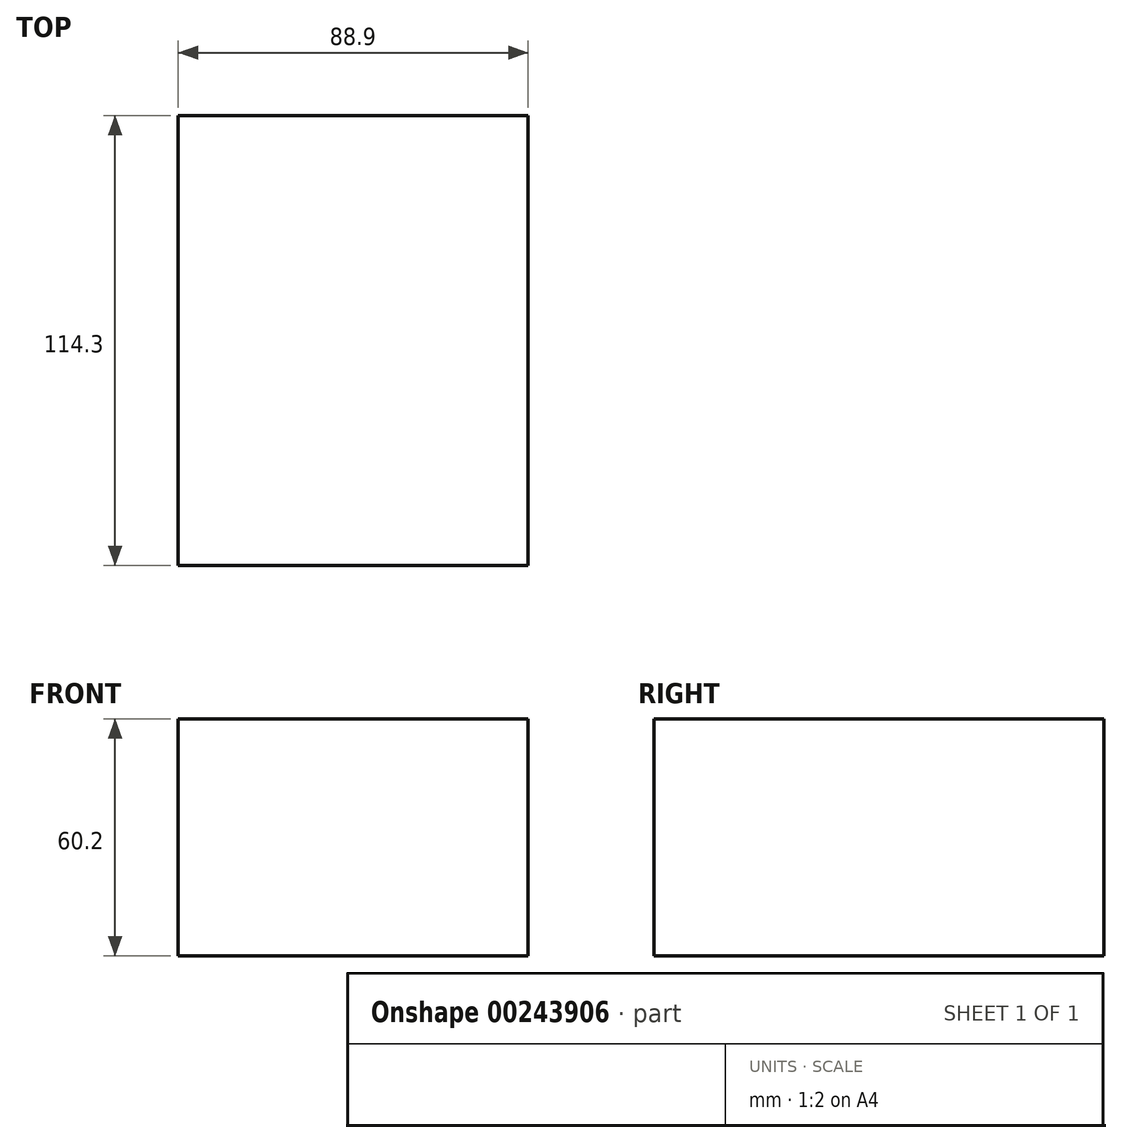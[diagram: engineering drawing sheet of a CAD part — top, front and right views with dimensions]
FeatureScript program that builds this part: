
annotation { "Feature Type Name" : "Feature", "Feature Type Description" : "" }
export const myFeature = defineFeature(function(context is Context, id is Id, definition is map)
    precondition{}
    {
        {
            var Q0;
            Q0=qCreatedBy(makeId("Top.planeOp"),FACE);
            var sketch = newSketch(context, id + "F0", { "sketchPlane" : qUnion([Q0])});
            skLineSegment(sketch, "E0.bottom", {"start": v(-25.4, -58.42) * mm, "end": v(63.5, -58.42) * mm});
            skLineSegment(sketch, "E0.top", {"start": v(-25.4, 55.88) * mm, "end": v(63.5, 55.88) * mm});
            skLineSegment(sketch, "E0.left", {"start": v(-25.4, -58.42) * mm, "end": v(-25.4, 55.88) * mm});
            skLineSegment(sketch, "E0.right", {"start": v(63.5, -58.42) * mm, "end": v(63.5, 55.88) * mm});
            skSolve(sketch);
        }
        {
            var Q0;
            Q0=makeQuery(id+"F0.imprint","IMPRINT",FACE,{"disambiguationData":[TD([[makeQuery(id+"F0.imprint","IMPRINT",EDGE,{"derivedFrom":sQuery(id+"F0.wireOp",EDGE,"E0.bottom")}),1.0]])]});
            extrude(context, id + "F1", {"entities" : qUnion([Q0]), "depth" : 60.2 * mm});
        }
    });
